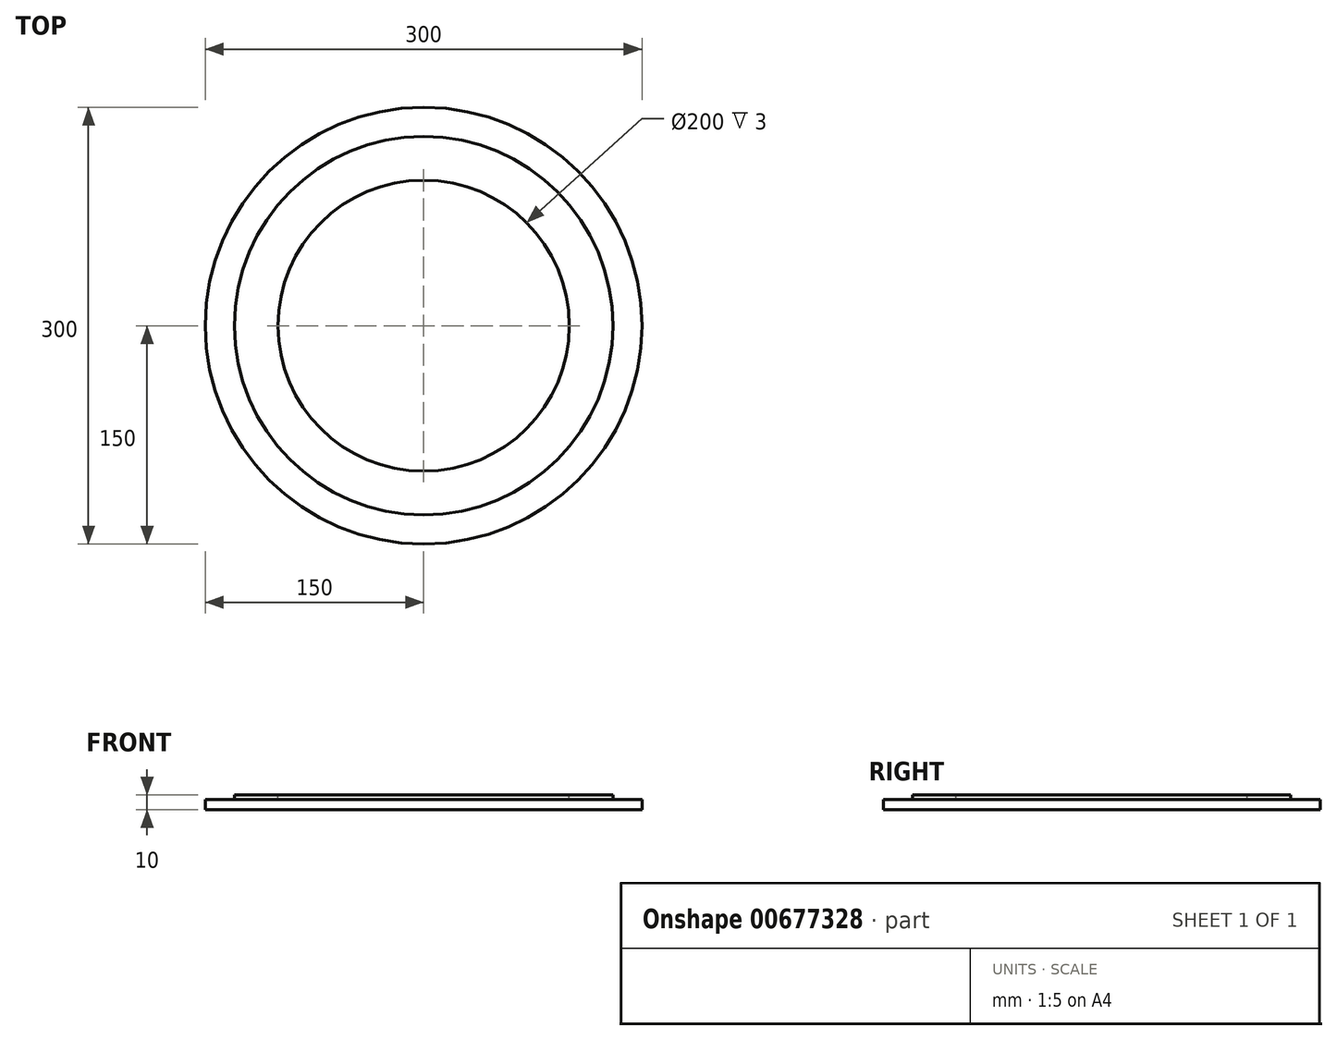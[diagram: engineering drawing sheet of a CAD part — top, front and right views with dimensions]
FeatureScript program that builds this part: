
annotation { "Feature Type Name" : "Feature", "Feature Type Description" : "" }
export const myFeature = defineFeature(function(context is Context, id is Id, definition is map)
    precondition{}
    {
        {
            var Q0;
            Q0=qCreatedBy(makeId("Top.planeOp"),FACE);
            var sketch = newSketch(context, id + "F0", { "sketchPlane" : qUnion([Q0])});
            skCircle(sketch, "E0", {"center": v(0, 0) * mm, "radius": 150 * mm});
            skSolve(sketch);
        }
        {
            var Q0;
            Q0 = qSketchRegion(id + "F0", true);
            extrude(context, id + "F1", {"entities" : qUnion([Q0]), "depth" : 10 * mm, "offsetDistance" : 25 * mm});
        }
        {
            var Q0;
            Q0=makeQuery(id+"F1.opExtrude","CAP_FACE",FACE,{"disambiguationData":[OSD([sQuery(id+"F0.wireOp",EDGE,"E0")])],"isStart":false});
            var sketch = newSketch(context, id + "F2", { "sketchPlane" : qUnion([Q0])});
            skCircle(sketch, "E1", {"center": v(0, 0) * mm, "radius": 100 * mm});
            skCircle(sketch, "E2", {"center": v(0, 0) * mm, "radius": 130 * mm});
            skSolve(sketch);
        }
        {
            var Q0;
            Q0=makeQuery(id+"F2.imprint","IMPRINT",FACE,{"disambiguationData":[TD([[makeQuery(id+"F2.imprint","IMPRINT",EDGE,{"derivedFrom":sQuery(id+"F2.wireOp",EDGE,"E1")}),1.0]])]});
            var Q1;
            Q1=makeQuery(id+"F2.imprint","IMPRINT",FACE,{"disambiguationData":[TD([[makeQuery(id+"F2.imprint","IMPRINT",EDGE,{"derivedFrom":sQuery(id+"F2.wireOp",EDGE,"E2")}),-1.0]])]});
            extrude(context, id + "F3", {"entities" : qUnion([Q0, Q1]), "operationType" : NewBodyOperationType.REMOVE, "oppositeDirection" : true, "depth" : 3 * mm, "offsetDistance" : 25 * mm});
        }
    });
